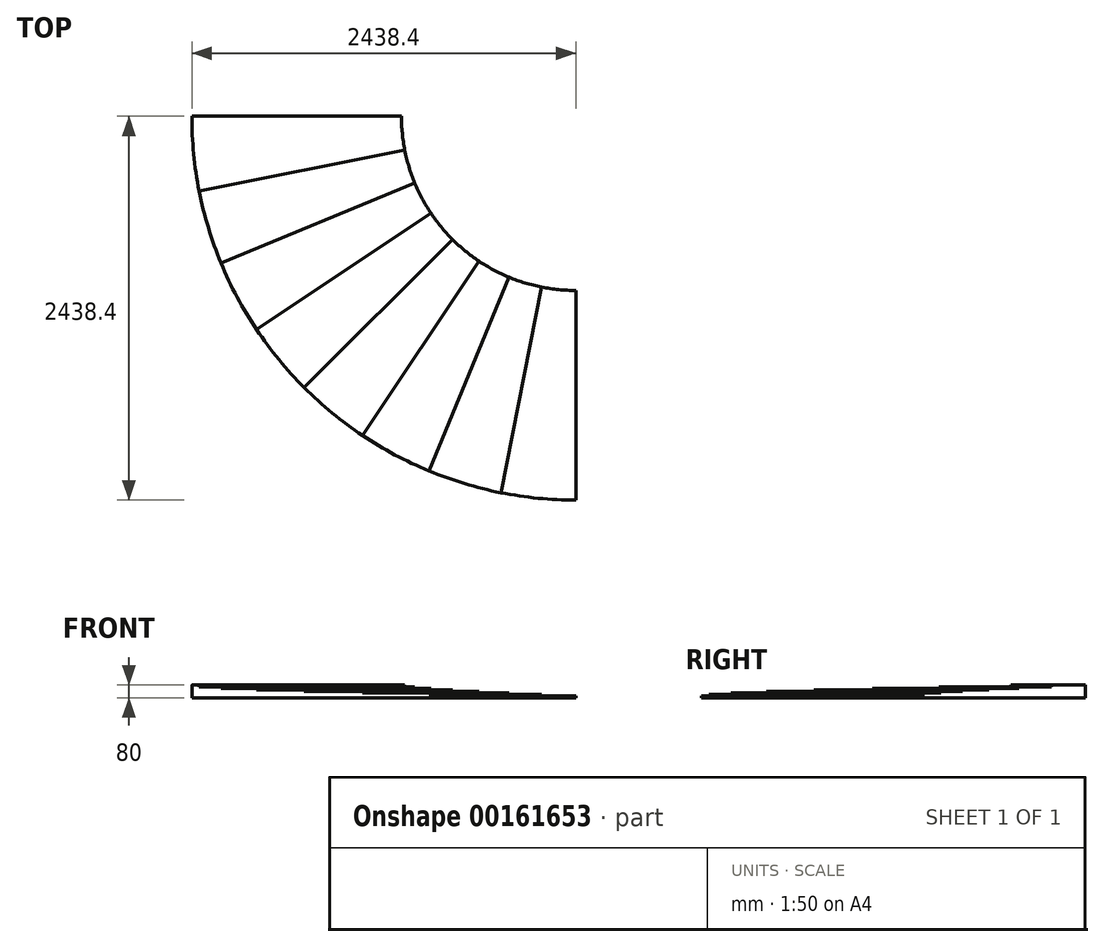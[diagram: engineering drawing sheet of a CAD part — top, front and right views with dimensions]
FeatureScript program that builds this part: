
annotation { "Feature Type Name" : "Feature", "Feature Type Description" : "" }
export const myFeature = defineFeature(function(context is Context, id is Id, definition is map)
    precondition{}
    {
        {
            assignVariable(context, id + "F0", {"name" : "StepHeight", "anyValue" : 10});
        }
        {
            var Q0;
            Q0=qCreatedBy(makeId("Top.planeOp"),FACE);
            var sketch = newSketch(context, id + "F1", { "sketchPlane" : qUnion([Q0])});
            skLineSegment(sketch, "E0", {"start": v(0, 0) * mm, "end": v(0, -1331.38) * mm, "construction": true});
            skLineSegment(sketch, "E1", {"start": v(0, -1331.38) * mm, "end": v(-979.53, -1331.38) * mm, "construction": true});
            skLineSegment(sketch, "E2", {"start": v(-979.53, -1331.38) * mm, "end": v(-3417.93, 1107.02) * mm, "construction": true});
            skLineSegment(sketch, "E3", {"start": v(-3417.93, 1107.02) * mm, "end": v(-3417.93, 2307.05) * mm, "construction": true});
            skLineSegment(sketch, "E4", {"start": v(-3417.93, 2307.05) * mm, "end": v(-2086.54, 2307.05) * mm, "construction": true});
            skLineSegment(sketch, "E5", {"start": v(-2086.54, 2307.05) * mm, "end": v(-2086.54, 1107.02) * mm, "construction": true});
            skLineSegment(sketch, "E6", {"start": v(-2086.54, 1107.02) * mm, "end": v(-979.53, 0) * mm, "construction": true});
            skLineSegment(sketch, "E7", {"start": v(-979.53, 0) * mm, "end": v(0, 0) * mm, "construction": true});
            skArc(sketch, "E8", {"start": v(-3417.93, 1107.02) * mm, "mid": v(-2703.74, -617.2) * mm, "end": v(-979.53, -1331.38) * mm, "construction": true});
            skArc(sketch, "E9", {"start": v(-2086.54, 1107.02) * mm, "mid": v(-1762.3, 324.24) * mm, "end": v(-979.53, 0) * mm, "construction": true});
            skSolve(sketch);
        }
        {
            var Q0;
            Q0=qCreatedBy(makeId("Top.planeOp"),FACE);
            var sketch = newSketch(context, id + "F2", { "sketchPlane" : qUnion([Q0])});
            skLineSegment(sketch, "E10", {"start": v(-979.53, 0) * mm, "end": v(-979.53, -1331.38) * mm});
            skLineSegment(sketch, "E11", {"start": v(-1455.24, -1284.53) * mm, "end": v(-1195.5, 21.27) * mm});
            skArc(sketch, "E12", {"start": v(-1195.5, 21.27) * mm, "mid": v(-1088.03, 5.33) * mm, "end": v(-979.53, 0) * mm});
            skArc(sketch, "E13", {"start": v(-1455.24, -1284.53) * mm, "mid": v(-1218.53, -1319.64) * mm, "end": v(-979.53, -1331.38) * mm});
            skLineSegment(sketch, "E14", {"start": v(-979.53, -1331.38) * mm, "end": v(-1455.24, -1284.53) * mm, "construction": true});
            skLineSegment(sketch, "E15", {"start": v(-1325.37, -631.63) * mm, "end": v(-979.53, -665.7) * mm, "construction": true});
            skSolve(sketch);
        }
        {
            var Q0;
            Q0=qCreatedBy(makeId("Top.planeOp"),FACE);
            var sketch = newSketch(context, id + "F3", { "sketchPlane" : qUnion([Q0])});
            skLineSegment(sketch, "E16", {"start": v(-1195.5, 21.27) * mm, "end": v(-1455.24, -1284.53) * mm});
            skLineSegment(sketch, "E17", {"start": v(-1912.66, -1145.77) * mm, "end": v(-1403.16, 84.27) * mm});
            skArc(sketch, "E18", {"start": v(-1403.16, 84.27) * mm, "mid": v(-1300.88, 47.67) * mm, "end": v(-1195.5, 21.27) * mm});
            skArc(sketch, "E19", {"start": v(-1912.66, -1145.77) * mm, "mid": v(-1687.36, -1226.39) * mm, "end": v(-1455.24, -1284.53) * mm});
            skLineSegment(sketch, "E20", {"start": v(-1455.24, -1284.53) * mm, "end": v(-1912.66, -1145.77) * mm, "construction": true});
            skSolve(sketch);
        }
        {
            var Q0;
            Q0=qCreatedBy(makeId("Top.planeOp"),FACE);
            var sketch = newSketch(context, id + "F4", { "sketchPlane" : qUnion([Q0])});
            skLineSegment(sketch, "E21", {"start": v(-1403.16, 84.27) * mm, "end": v(-1912.66, -1145.77) * mm});
            skLineSegment(sketch, "E22", {"start": v(-2334.23, -920.44) * mm, "end": v(-1594.55, 186.57) * mm});
            skArc(sketch, "E23", {"start": v(-1594.55, 186.57) * mm, "mid": v(-1501.37, 130.72) * mm, "end": v(-1403.16, 84.27) * mm});
            skArc(sketch, "E24", {"start": v(-2334.23, -920.44) * mm, "mid": v(-2128.98, -1043.46) * mm, "end": v(-1912.66, -1145.77) * mm});
            skLineSegment(sketch, "E25", {"start": v(-1912.66, -1145.77) * mm, "end": v(-2334.23, -920.44) * mm, "construction": true});
            skSolve(sketch);
        }
        {
            var Q0;
            Q0=qCreatedBy(makeId("Top.planeOp"),FACE);
            var sketch = newSketch(context, id + "F5", { "sketchPlane" : qUnion([Q0])});
            skLineSegment(sketch, "E26", {"start": v(-1594.55, 186.57) * mm, "end": v(-2334.23, -920.44) * mm});
            skLineSegment(sketch, "E27", {"start": v(-2703.74, -617.2) * mm, "end": v(-1762.3, 324.24) * mm});
            skArc(sketch, "E28", {"start": v(-1762.3, 324.24) * mm, "mid": v(-1681.81, 251.28) * mm, "end": v(-1594.55, 186.57) * mm});
            skArc(sketch, "E29", {"start": v(-2703.74, -617.2) * mm, "mid": v(-2526.43, -777.9) * mm, "end": v(-2334.23, -920.44) * mm});
            skLineSegment(sketch, "E30", {"start": v(-2334.23, -920.44) * mm, "end": v(-2703.74, -617.2) * mm, "construction": true});
            skSolve(sketch);
        }
        {
            var Q0;
            Q0=qCreatedBy(makeId("Top.planeOp"),FACE);
            var sketch = newSketch(context, id + "F6", { "sketchPlane" : qUnion([Q0])});
            skLineSegment(sketch, "E31", {"start": v(-1762.3, 324.24) * mm, "end": v(-2703.74, -617.2) * mm});
            skLineSegment(sketch, "E32", {"start": v(-3006.98, -247.69) * mm, "end": v(-1899.98, 492) * mm});
            skArc(sketch, "E33", {"start": v(-1899.98, 492) * mm, "mid": v(-1835.26, 404.73) * mm, "end": v(-1762.3, 324.24) * mm});
            skArc(sketch, "E34", {"start": v(-3006.98, -247.69) * mm, "mid": v(-2864.44, -439.89) * mm, "end": v(-2703.74, -617.2) * mm});
            skLineSegment(sketch, "E35", {"start": v(-2703.74, -617.2) * mm, "end": v(-3006.98, -247.69) * mm, "construction": true});
            skSolve(sketch);
        }
        {
            var Q0;
            Q0=qCreatedBy(makeId("Top.planeOp"),FACE);
            var sketch = newSketch(context, id + "F7", { "sketchPlane" : qUnion([Q0])});
            skLineSegment(sketch, "E36", {"start": v(-1899.98, 492) * mm, "end": v(-3006.98, -247.69) * mm});
            skLineSegment(sketch, "E37", {"start": v(-3232.31, 173.88) * mm, "end": v(-2002.28, 683.38) * mm});
            skArc(sketch, "E38", {"start": v(-2002.28, 683.38) * mm, "mid": v(-1955.83, 585.17) * mm, "end": v(-1899.98, 492) * mm});
            skArc(sketch, "E39", {"start": v(-3232.31, 173.88) * mm, "mid": v(-3130, -42.44) * mm, "end": v(-3006.98, -247.69) * mm});
            skLineSegment(sketch, "E40", {"start": v(-3006.98, -247.69) * mm, "end": v(-3232.31, 173.88) * mm, "construction": true});
            skSolve(sketch);
        }
        {
            var Q0;
            Q0=qCreatedBy(makeId("Top.planeOp"),FACE);
            var sketch = newSketch(context, id + "F8", { "sketchPlane" : qUnion([Q0])});
            skLineSegment(sketch, "E41", {"start": v(-2002.28, 683.38) * mm, "end": v(-3232.31, 173.88) * mm});
            skLineSegment(sketch, "E42", {"start": v(-3371.07, 631.3) * mm, "end": v(-2065.27, 891.05) * mm});
            skArc(sketch, "E43", {"start": v(-2065.27, 891.05) * mm, "mid": v(-2038.88, 785.67) * mm, "end": v(-2002.28, 683.38) * mm});
            skArc(sketch, "E44", {"start": v(-3371.07, 631.3) * mm, "mid": v(-3312.93, 399.19) * mm, "end": v(-3232.31, 173.88) * mm});
            skLineSegment(sketch, "E45", {"start": v(-3232.31, 173.88) * mm, "end": v(-3371.07, 631.3) * mm, "construction": true});
            skSolve(sketch);
        }
        {
            var Q0;
            Q0=qCreatedBy(makeId("Top.planeOp"),FACE);
            var sketch = newSketch(context, id + "F9", { "sketchPlane" : qUnion([Q0])});
            skLineSegment(sketch, "E46", {"start": v(-2065.27, 891.05) * mm, "end": v(-3371.07, 631.3) * mm});
            skLineSegment(sketch, "E47", {"start": v(-3417.93, 1107.02) * mm, "end": v(-2086.54, 1107.02) * mm});
            skArc(sketch, "E48", {"start": v(-2086.54, 1107.02) * mm, "mid": v(-2081.21, 998.51) * mm, "end": v(-2065.27, 891.05) * mm});
            skArc(sketch, "E49", {"start": v(-3417.93, 1107.02) * mm, "mid": v(-3406.19, 868.01) * mm, "end": v(-3371.07, 631.3) * mm});
            skLineSegment(sketch, "E50", {"start": v(-3371.07, 631.3) * mm, "end": v(-3417.93, 1107.02) * mm, "construction": true});
            skSolve(sketch);
        }
        {
            var Q0;
            Q0 = qSketchRegion(id + "F2", true);
            extrude(context, id + "F10", {"entities" : qUnion([Q0]), "depth" : (getVariable(context, 'StepHeight')) * mm});
        }
        {
            var Q0;
            Q0 = qSketchRegion(id + "F3", true);
            extrude(context, id + "F11", {"entities" : qUnion([Q0]), "operationType" : NewBodyOperationType.ADD, "depth" : (getVariable(context, 'StepHeight') * 2) * mm});
        }
        {
            var Q0;
            Q0 = qSketchRegion(id + "F4", true);
            extrude(context, id + "F12", {"entities" : qUnion([Q0]), "operationType" : NewBodyOperationType.ADD, "depth" : (getVariable(context, 'StepHeight') * 3) * mm});
        }
        {
            var Q0;
            Q0 = qSketchRegion(id + "F5", true);
            extrude(context, id + "F13", {"entities" : qUnion([Q0]), "operationType" : NewBodyOperationType.ADD, "depth" : (getVariable(context, 'StepHeight') * 4) * mm});
        }
        {
            var Q0;
            Q0 = qSketchRegion(id + "F6", true);
            extrude(context, id + "F14", {"entities" : qUnion([Q0]), "operationType" : NewBodyOperationType.ADD, "depth" : (getVariable(context, 'StepHeight') * 5) * mm});
        }
        {
            var Q0;
            Q0 = qSketchRegion(id + "F7", true);
            extrude(context, id + "F15", {"entities" : qUnion([Q0]), "operationType" : NewBodyOperationType.ADD, "depth" : (getVariable(context, 'StepHeight') * 6) * mm});
        }
        {
            var Q0;
            Q0 = qSketchRegion(id + "F8", true);
            extrude(context, id + "F16", {"entities" : qUnion([Q0]), "operationType" : NewBodyOperationType.ADD, "depth" : (getVariable(context, 'StepHeight') * 7) * mm});
        }
        {
            var Q0;
            Q0 = qSketchRegion(id + "F9", true);
            extrude(context, id + "F17", {"entities" : qUnion([Q0]), "operationType" : NewBodyOperationType.ADD, "depth" : (getVariable(context, 'StepHeight') * 8) * mm});
        }
    });
